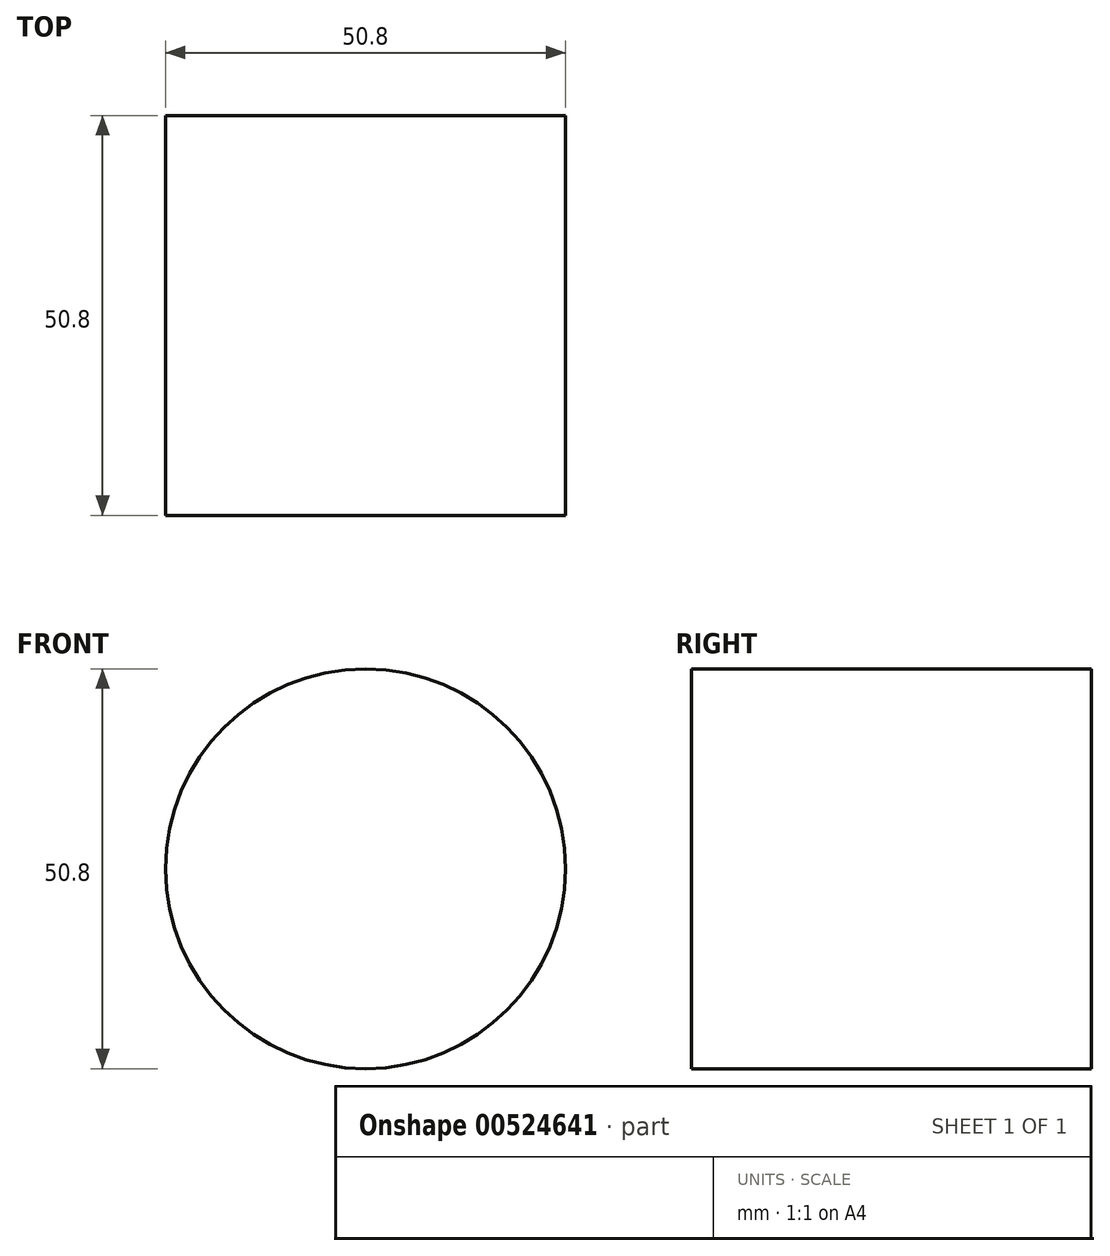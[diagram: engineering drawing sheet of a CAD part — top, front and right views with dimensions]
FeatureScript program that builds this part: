
annotation { "Feature Type Name" : "Feature", "Feature Type Description" : "" }
export const myFeature = defineFeature(function(context is Context, id is Id, definition is map)
    precondition{}
    {
        {
            var Q0;
            Q0=qCreatedBy(makeId("Front.planeOp"),FACE);
            var sketch = newSketch(context, id + "F0", { "sketchPlane" : qUnion([Q0])});
            skCircle(sketch, "E0", {"center": v(0, 0) * mm, "radius": 25.4 * mm});
            skArc(sketch, "E1", {"start": v(0, 44.05) * mm, "mid": v(-9.35, 34.73) * mm, "end": v(-12.75, 21.97) * mm});
            skLineSegment(sketch, "E2", {"start": v(0, 0) * mm, "end": v(0, 47.41) * mm, "construction": true});
            skArc(sketch, "E3.1.0", {"start": v(-41.9, 13.61) * mm, "mid": v(-35.92, 1.84) * mm, "end": v(-24.83, -5.34) * mm});
            skArc(sketch, "E3.2.0", {"start": v(-25.9, -35.64) * mm, "mid": v(-12.85, -33.59) * mm, "end": v(-2.6, -25.27) * mm});
            skArc(sketch, "E3.3.0", {"start": v(25.9, -35.64) * mm, "mid": v(27.97, -22.6) * mm, "end": v(23.23, -10.28) * mm});
            skArc(sketch, "E3.4.0", {"start": v(41.9, 13.61) * mm, "mid": v(30.14, 19.62) * mm, "end": v(16.95, 18.92) * mm});
            skArc(sketch, "E3.4.2", {"start": v(41.9, 13.61) * mm, "mid": v(35.92, 1.84) * mm, "end": v(24.83, -5.34) * mm});
            skPoint(sketch, "E4.orphan", {"position": v(12.62, 47.43) * mm});
            skArc(sketch, "E5.trimOffspring", {"start": v(0, 44.05) * mm, "mid": v(9.35, 34.73) * mm, "end": v(12.75, 21.97) * mm});
            skPoint(sketch, "E6.orphan", {"position": v(40.78, 27.86) * mm});
            skPoint(sketch, "E7.orphan", {"position": v(49, 2.65) * mm});
            skPoint(sketch, "E8.orphan", {"position": v(17.67, -45.79) * mm});
            skArc(sketch, "E9.trimOffspring", {"start": v(25.9, -35.64) * mm, "mid": v(12.85, -33.59) * mm, "end": v(2.6, -25.27) * mm});
            skArc(sketch, "E10.trimOffspring", {"start": v(-25.9, -35.64) * mm, "mid": v(-27.97, -22.6) * mm, "end": v(-23.23, -10.28) * mm});
            skPoint(sketch, "E11.orphan", {"position": v(-38.09, -30.95) * mm});
            skArc(sketch, "E12.trimOffspring", {"start": v(-41.9, 13.61) * mm, "mid": v(-30.14, 19.62) * mm, "end": v(-16.95, 18.92) * mm});
            skPoint(sketch, "E13.orphan", {"position": v(-41.2, 26.66) * mm});
            skSolve(sketch);
        }
        {
            var Q0;
            {var subQ0=sQuery(id+"F0.wireOp",EDGE,"E0");var subQ5=makeQuery(id+"F0.imprint","INTERSECT",VERTEX,{"derivedFrom":[subQ0,sQuery(id+"F0.wireOp",EDGE,"E3.4.0")]});Q0=makeQuery(id+"F0.imprint","IMPRINT",FACE,{"disambiguationData":[TD([[makeQuery(id+"F0.imprint","IMPRINT",EDGE,{"disambiguationData":[TD([[subQ5,-1.0]])],"derivedFrom":subQ0}),1.0]])]});}
            var Q1;
            {var subQ0=sQuery(id+"F0.wireOp",EDGE,"E3.1.0");Q1=makeQuery(id+"F0.imprint","IMPRINT",FACE,{"disambiguationData":[TD([[makeQuery(id+"F0.imprint","IMPRINT",EDGE,{"derivedFrom":subQ0}),-1.0]])]});}
            var Q2;
            {var subQ0=sQuery(id+"F0.wireOp",EDGE,"E1");Q2=makeQuery(id+"F0.imprint","IMPRINT",FACE,{"disambiguationData":[TD([[makeQuery(id+"F0.imprint","IMPRINT",EDGE,{"derivedFrom":subQ0}),-1.0]])]});}
            var Q3;
            {var subQ0=sQuery(id+"F0.wireOp",EDGE,"E3.4.0");Q3=makeQuery(id+"F0.imprint","IMPRINT",FACE,{"disambiguationData":[TD([[makeQuery(id+"F0.imprint","IMPRINT",EDGE,{"derivedFrom":subQ0}),-1.0]])]});}
            var Q4;
            {var subQ0=sQuery(id+"F0.wireOp",EDGE,"E3.3.0");Q4=makeQuery(id+"F0.imprint","IMPRINT",FACE,{"disambiguationData":[TD([[makeQuery(id+"F0.imprint","IMPRINT",EDGE,{"derivedFrom":subQ0}),-1.0]])]});}
            var Q5;
            {var subQ0=sQuery(id+"F0.wireOp",EDGE,"E3.2.0");Q5=makeQuery(id+"F0.imprint","IMPRINT",FACE,{"disambiguationData":[TD([[makeQuery(id+"F0.imprint","IMPRINT",EDGE,{"derivedFrom":subQ0}),-1.0]])]});}
            extrude(context, id + "F1", {"entities" : qUnion([Q0, Q1, Q2, Q3, Q4, Q5]), "depth" : 50.8 * mm, "offsetDistance" : 25.4 * mm});
        }
    });
